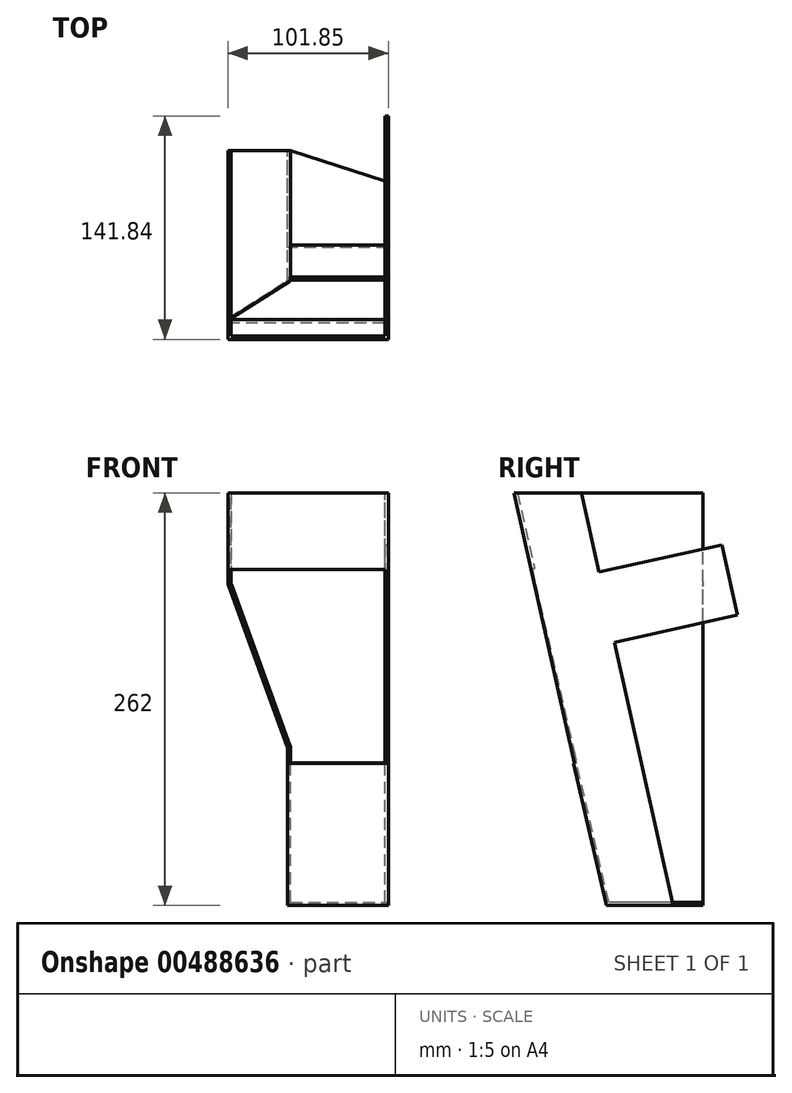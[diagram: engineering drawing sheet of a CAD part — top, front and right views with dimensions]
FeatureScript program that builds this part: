
annotation { "Feature Type Name" : "Feature", "Feature Type Description" : "" }
export const myFeature = defineFeature(function(context is Context, id is Id, definition is map)
    precondition{}
    {
        {
            var Q0;
            Q0=qCreatedBy(makeId("Front.planeOp"),FACE);
            var sketch = newSketch(context, id + "F0", { "sketchPlane" : qUnion([Q0])});
            skLineSegment(sketch, "E0", {"start": v(0, 0) * mm, "end": v(0, 100.23) * mm});
            skLineSegment(sketch, "E1", {"start": v(0, 100.23) * mm, "end": v(-37.85, 204.21) * mm});
            skLineSegment(sketch, "E2", {"start": v(-37.85, 204.21) * mm, "end": v(-37.85, 262) * mm});
            skLineSegment(sketch, "E3", {"start": v(-37.85, 262) * mm, "end": v(-35.85, 262) * mm});
            skLineSegment(sketch, "E4", {"start": v(0, 0) * mm, "end": v(2, 0) * mm});
            skLineSegment(sketch, "E5.0", {"start": v(-31.5, 204.21) * mm, "end": v(-31.5, 262) * mm});
            skLineSegment(sketch, "E6.0", {"start": v(-35.85, 204.56) * mm, "end": v(-35.85, 262) * mm});
            skLineSegment(sketch, "E6.1", {"start": v(2, 100.58) * mm, "end": v(-35.85, 204.56) * mm});
            skLineSegment(sketch, "E6.2", {"start": v(2, 0) * mm, "end": v(2, 100.58) * mm});
            skSolve(sketch);
        }
        {
            var Q0;
            Q0 = qSketchRegion(id + "F0", true);
            extrude(context, id + "F1", {"entities" : qUnion([Q0]), "endBound" : BoundingType.SYMMETRIC, "depth" : 120 * mm});
        }
        {
            var Q0;
            Q0=makeQuery(id+"F1.opExtrude","SWEPT_FACE",FACE,{"disambiguationData":[OSD([sQuery(id+"F0.wireOp",EDGE,"E0")])]});
            var sketch = newSketch(context, id + "F2", { "sketchPlane" : qUnion([Q0])});
            skLineSegment(sketch, "E7", {"start": v(1.51, 0) * mm, "end": v(22.3, 90.04) * mm});
            skPoint(sketch, "E7.endSnap0", {"position": v(60, 50.12) * mm});
            skLineSegment(sketch, "E8", {"start": v(1.51, 0) * mm, "end": v(-0.49, 0) * mm});
            skLineSegment(sketch, "E9", {"start": v(-0.5, 0) * mm, "end": v(20.4, 90.48) * mm});
            skLineSegment(sketch, "E10", {"start": v(22.3, 90.04) * mm, "end": v(20.4, 90.48) * mm});
            skPoint(sketch, "E11.orphan", {"position": v(60, 253.35) * mm});
            skPoint(sketch, "E12.orphan", {"position": v(60, 262.01) * mm});
            skSolve(sketch);
        }
        {
            var Q0;
            Q0 = qSketchRegion(id + "F2", true);
            extrude(context, id + "F3", {"entities" : qUnion([Q0]), "operationType" : NewBodyOperationType.ADD, "oppositeDirection" : true, "depth" : 64 * mm});
        }
        {
            var Q0;
            Q0=makeQuery(id+"F1.opExtrude","SWEPT_EDGE",EDGE,{"disambiguationData":[OSD([sQuery(id+"F0.wireOp",EDGE,"E6.1"),sQuery(id+"F0.wireOp",EDGE,"E6.2")])]});
            var Q1;
            Q1=makeQuery(id+"F1.opExtrude","SWEPT_EDGE",EDGE,{"disambiguationData":[OSD([sQuery(id+"F0.wireOp",EDGE,"E6.0"),sQuery(id+"F0.wireOp",EDGE,"E6.1")])]});
            var Q2;
            Q2=makeQuery(id+"F1.opExtrude","SWEPT_EDGE",EDGE,{"disambiguationData":[OSD([sQuery(id+"F0.wireOp",EDGE,"E1"),sQuery(id+"F0.wireOp",EDGE,"E2")])]});
            var Q3;
            Q3=makeQuery(id+"F1.opExtrude","SWEPT_EDGE",EDGE,{"disambiguationData":[OSD([sQuery(id+"F0.wireOp",EDGE,"E0"),sQuery(id+"F0.wireOp",EDGE,"E1")])]});
            fillet(context, id + "F4", {"entities" : qUnion([Q0, Q1, Q2, Q3]), "radius" : 5.08 * mm, "tangentPropagation" : true, "allowEdgeOverflow" : false});
        }
        {
            var Q0;
            Q0=makeQuery(id+"F1.opExtrude","SWEPT_FACE",FACE,{"disambiguationData":[OSD([sQuery(id+"F0.wireOp",EDGE,"E6.2")])]});
            var sketch = newSketch(context, id + "F5", { "sketchPlane" : qUnion([Q0])});
            skLineSegment(sketch, "E13", {"start": v(-20.4, 90.48) * mm, "end": v(-60.76, 265.32) * mm});
            skLineSegment(sketch, "E14", {"start": v(-60.76, 265.32) * mm, "end": v(-60, 0) * mm});
            skLineSegment(sketch, "E15", {"start": v(-60, 0) * mm, "end": v(-1.51, 0) * mm});
            skSolve(sketch);
        }
        {
            var Q0;
            Q0=makeQuery(id+"F5.imprint","IMPRINT",FACE,{"disambiguationData":[TD([[makeQuery(id+"F5.imprint","IMPRINT",EDGE,{"derivedFrom":sQuery(id+"F5.wireOp",EDGE,"E15")}),1.0]])]});
            var Q1;
            {var subQ0=sQuery(id+"F5.wireOp",EDGE,"E14");Q1=makeQuery(id+"F5.imprint","IMPRINT",FACE,{"disambiguationData":[TD([[makeQuery(id+"F5.imprint","IMPRINT",EDGE,{"derivedFrom":subQ0}),1.0]])]});}
            extrude(context, id + "F6", {"entities" : qUnion([Q0, Q1]), "operationType" : NewBodyOperationType.REMOVE, "endBound" : BoundingType.THROUGH_ALL, "oppositeDirection" : true, "depth" : 25.4 * mm});
        }
        {
            var Q0;
            Q0=makeQuery(id+"F1.opExtrude","SWEPT_FACE",FACE,{"disambiguationData":[OSD([sQuery(id+"F0.wireOp",EDGE,"E0")])]});
            var sketch = newSketch(context, id + "F7", { "sketchPlane" : qUnion([Q0])});
            skLineSegment(sketch, "E16", {"start": v(-60, 0) * mm, "end": v(-60, 2) * mm});
            skLineSegment(sketch, "E17", {"start": v(-60, 2) * mm, "end": v(1.97, 2) * mm});
            skLineSegment(sketch, "E18", {"start": v(1.97, 2) * mm, "end": v(1.51, 0) * mm});
            skLineSegment(sketch, "E19", {"start": v(1.51, 0) * mm, "end": v(-60, 0) * mm});
            skSolve(sketch);
        }
        {
            var Q0;
            Q0 = qSketchRegion(id + "F7", true);
            extrude(context, id + "F8", {"entities" : qUnion([Q0]), "operationType" : NewBodyOperationType.ADD, "oppositeDirection" : true, "depth" : 64 * mm});
        }
        {
            var Q0;
            Q0=makeQuery(id+"F8.boolean.opBoolean","MERGE",FACE,{"derivedFrom":[makeQuery(id+"F3.opExtrude","CAP_FACE",FACE,{"disambiguationData":[OSD([sQuery(id+"F2.wireOp",EDGE,"E7"),sQuery(id+"F2.wireOp",EDGE,"E8"),sQuery(id+"F2.wireOp",EDGE,"E9"),sQuery(id+"F2.wireOp",EDGE,"E10")])],"isStart":false}),makeQuery(id+"F8.opExtrude","CAP_FACE",FACE,{"disambiguationData":[OSD([sQuery(id+"F7.wireOp",EDGE,"E16"),sQuery(id+"F7.wireOp",EDGE,"E17"),sQuery(id+"F7.wireOp",EDGE,"E18"),sQuery(id+"F7.wireOp",EDGE,"E19")])],"isStart":false})]});
            var sketch = newSketch(context, id + "F9", { "sketchPlane" : qUnion([Q0])});
            skLineSegment(sketch, "E20", {"start": v(-1.51, 0) * mm, "end": v(41.05, 0) * mm});
            skLineSegment(sketch, "E21", {"start": v(41.05, 0) * mm, "end": v(3.77, 167.02) * mm});
            skLineSegment(sketch, "E22", {"start": v(3.77, 167.02) * mm, "end": v(81.84, 184.45) * mm});
            skLineSegment(sketch, "E23", {"start": v(81.84, 184.45) * mm, "end": v(71.88, 229.06) * mm});
            skLineSegment(sketch, "E24", {"start": v(71.88, 229.06) * mm, "end": v(-6.2, 211.63) * mm});
            skLineSegment(sketch, "E25", {"start": v(-6.2, 211.63) * mm, "end": v(-17.44, 262) * mm});
            skLineSegment(sketch, "E26", {"start": v(-17.44, 262) * mm, "end": v(-60, 262) * mm});
            skLineSegment(sketch, "E27", {"start": v(-60, 262) * mm, "end": v(-1.51, 0) * mm});
            skSolve(sketch);
        }
        {
            var Q0;
            Q0 = qSketchRegion(id + "F9", true);
            extrude(context, id + "F10", {"entities" : qUnion([Q0]), "operationType" : NewBodyOperationType.ADD, "oppositeDirection" : true, "depth" : 2 * mm});
        }
        {
            var Q0;
            Q0=makeQuery(id+"F10.boolean.opBoolean","MERGE",FACE,{"derivedFrom":[makeQuery(id+"F8.boolean.opBoolean","MERGE",FACE,{"derivedFrom":[makeQuery(id+"F3.opExtrude","CAP_FACE",FACE,{"disambiguationData":[OSD([sQuery(id+"F2.wireOp",EDGE,"E7"),sQuery(id+"F2.wireOp",EDGE,"E8"),sQuery(id+"F2.wireOp",EDGE,"E9"),sQuery(id+"F2.wireOp",EDGE,"E10")])],"isStart":false}),makeQuery(id+"F8.opExtrude","CAP_FACE",FACE,{"disambiguationData":[OSD([sQuery(id+"F7.wireOp",EDGE,"E16"),sQuery(id+"F7.wireOp",EDGE,"E17"),sQuery(id+"F7.wireOp",EDGE,"E18"),sQuery(id+"F7.wireOp",EDGE,"E19")])],"isStart":false})]}),makeQuery(id+"F10.opExtrude","CAP_FACE",FACE,{"disambiguationData":[OSD([sQuery(id+"F9.wireOp",EDGE,"E20"),sQuery(id+"F9.wireOp",EDGE,"E21"),sQuery(id+"F9.wireOp",EDGE,"E22"),sQuery(id+"F9.wireOp",EDGE,"E23"),sQuery(id+"F9.wireOp",EDGE,"E24"),sQuery(id+"F9.wireOp",EDGE,"E25"),sQuery(id+"F9.wireOp",EDGE,"E26"),sQuery(id+"F9.wireOp",EDGE,"E27")])],"isStart":true})]});
            var sketch = newSketch(context, id + "F11", { "sketchPlane" : qUnion([Q0])});
            skLineSegment(sketch, "E28", {"start": v(-60, 262) * mm, "end": v(-49.17, 213.51) * mm});
            skLineSegment(sketch, "E29", {"start": v(-49.17, 213.51) * mm, "end": v(-47.22, 213.95) * mm});
            skLineSegment(sketch, "E30", {"start": v(-47.22, 213.95) * mm, "end": v(-57.95, 262) * mm});
            skLineSegment(sketch, "E31", {"start": v(-57.95, 262) * mm, "end": v(-60, 262) * mm});
            skSolve(sketch);
        }
        {
            var Q0;
            Q0 = qSketchRegion(id + "F11", true);
            extrude(context, id + "F12", {"entities" : qUnion([Q0]), "operationType" : NewBodyOperationType.ADD, "oppositeDirection" : true, "depth" : 101.85 * mm});
        }
        {
            var Q0;
            Q0=makeQuery(id+"F8.opExtrude","SWEPT_FACE",FACE,{"disambiguationData":[OSD([sQuery(id+"F7.wireOp",EDGE,"E17")])]});
            var sketch = newSketch(context, id + "F13", { "sketchPlane" : qUnion([Q0])});
            skLineSegment(sketch, "E32", {"start": v(62, 40.6) * mm, "end": v(2, 60) * mm});
            skLineSegment(sketch, "E33", {"start": v(2, 60) * mm, "end": v(64, 60) * mm});
            skLineSegment(sketch, "E34", {"start": v(64, 60) * mm, "end": v(64, 40.6) * mm});
            skLineSegment(sketch, "E35", {"start": v(64, 40.6) * mm, "end": v(62, 40.6) * mm});
            skSolve(sketch);
        }
        {
            var Q0;
            Q0 = qSketchRegion(id + "F13", true);
            extrude(context, id + "F14", {"entities" : qUnion([Q0]), "operationType" : NewBodyOperationType.REMOVE, "endBound" : BoundingType.THROUGH_ALL, "oppositeDirection" : true, "depth" : 25.4 * mm});
        }
    });
